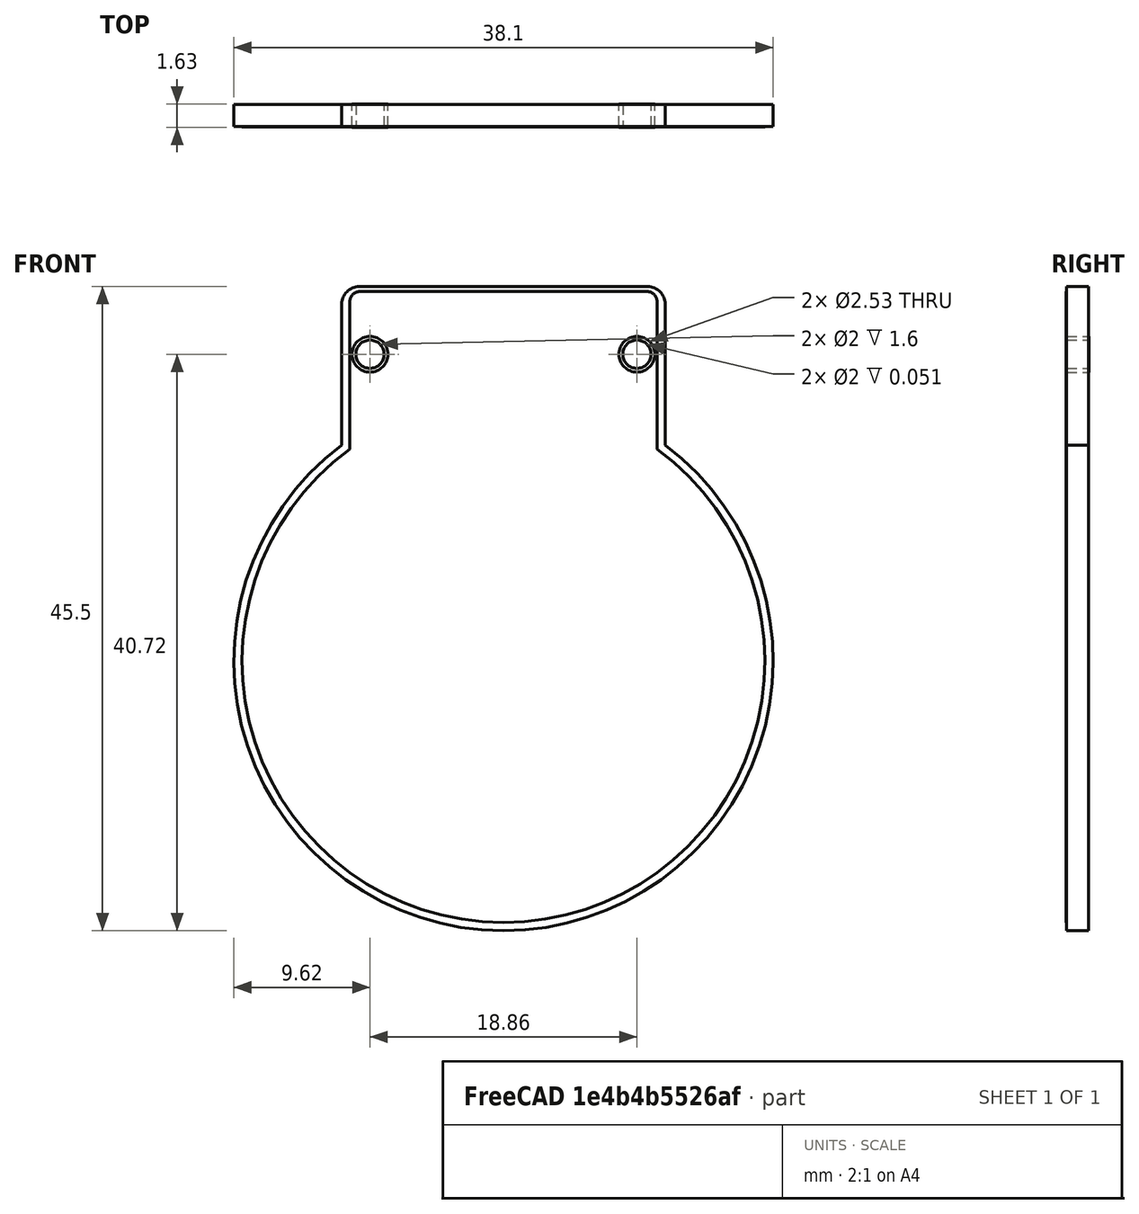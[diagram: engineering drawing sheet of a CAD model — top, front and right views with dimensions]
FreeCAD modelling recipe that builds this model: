
FCSTD DOCUMENT  (FreeCAD 1.0R39109 (Git))
Label: gc9a01
License: All rights reserved
objects: App::Link×2, Part::Feature×1, App::LinkGroup×1
note: 1 computed .brp shape members not serialized (recipe doc carries the construction recipe); baked Part::Feature solids carry a one-line shape summary decoded from their .brp
EXTERNAL_REF file=gc9a01_parts/TFT_Round_1_28_v1.fcstd obj=LinkGroup
EXTERNAL_REF file=gc9a01_parts/Component6.fcstd obj=LinkGroup

FEATURE [App::Link] Link  label="TFT-Round-1.28 v1"
  LinkPlacement = pos=(0,1.5875,-0.335) rot=(-1,0,0;1.5708rad)
  LinkedObject = -> <external gc9a01_parts/TFT_Round_1_28_v1.fcstd>#LinkGroup
  Placement = pos=(0,1.5875,-0.335) rot=(-1,0,0;1.5708rad)
FEATURE [App::Link] Link001  label="Component6"
  LinkedObject = -> <external gc9a01_parts/Component6.fcstd>#LinkGroup
FEATURE [Part::Feature] Compound
  shape: bbox 38.1 x 1.626 x 45.5 mm, 33 faces, 5 solids (baked)
FEATURE [App::LinkGroup] LinkGroup  label="Teyleten Robot 1.28 Inch GC9A01 240x240 v1"
  ElementList = -> [Link,Link001,Compound]
  LinkMode = 0
